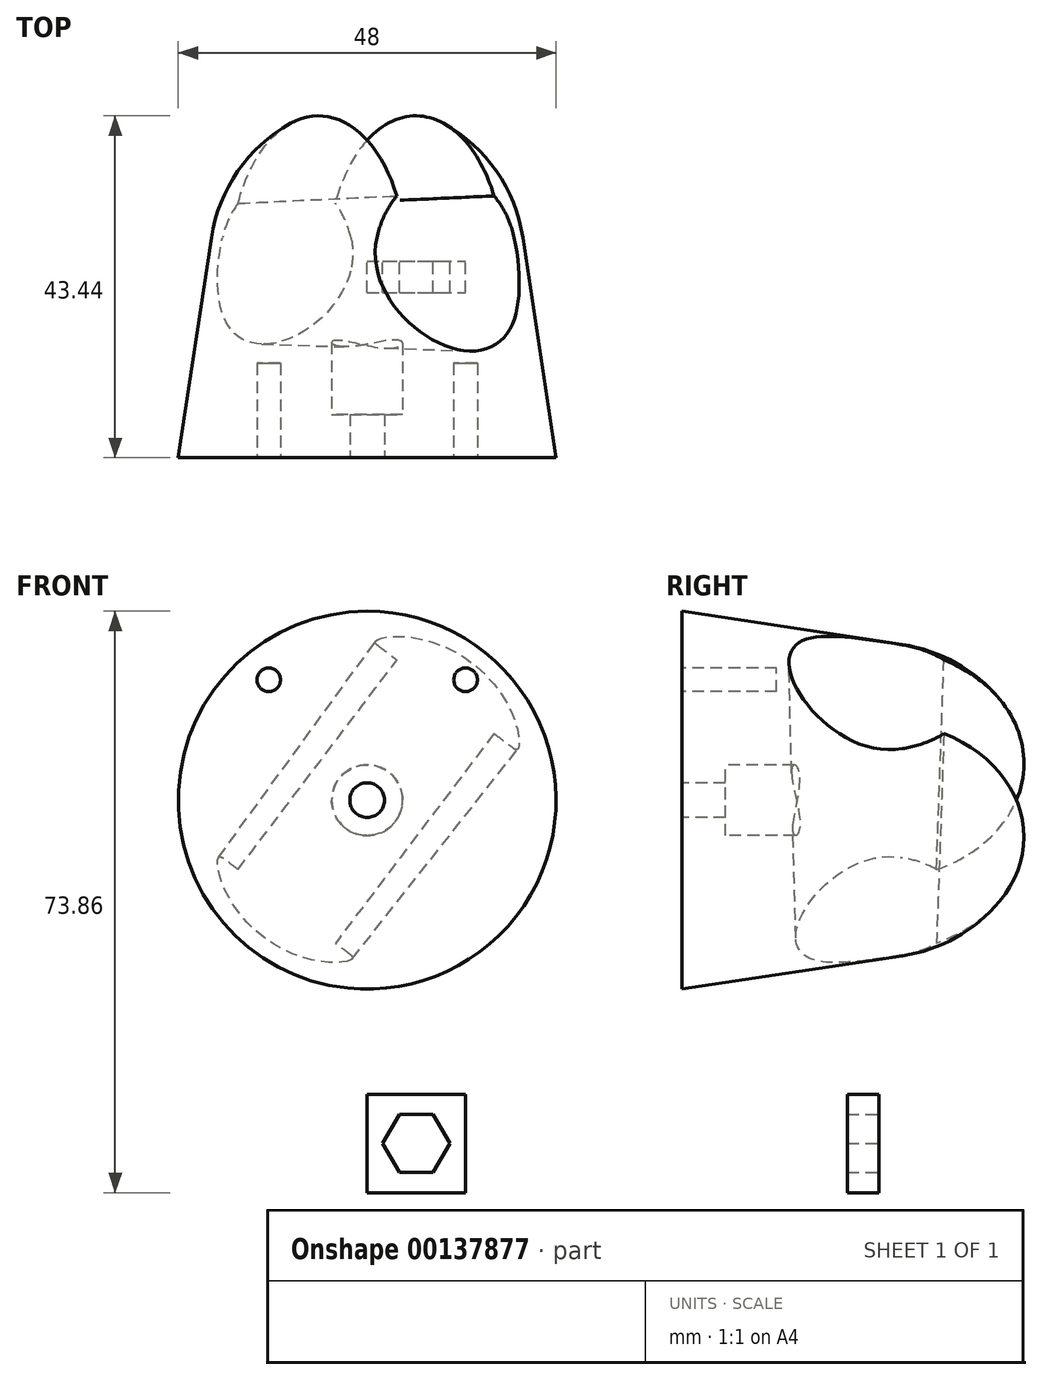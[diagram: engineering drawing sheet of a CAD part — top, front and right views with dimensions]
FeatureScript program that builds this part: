
annotation { "Feature Type Name" : "Feature", "Feature Type Description" : "" }
export const myFeature = defineFeature(function(context is Context, id is Id, definition is map)
    precondition{}
    {
        {
            var Q0;
            Q0=qCreatedBy(makeId("Front.planeOp"),FACE);
            var sketch = newSketch(context, id + "F0", { "sketchPlane" : qUnion([Q0])});
            skLineSegment(sketch, "E0", {"start": v(-15.1, -19.93) * mm, "end": v(15.1, 19.93) * mm});
            skLineSegment(sketch, "E1", {"start": v(15.1, 19.93) * mm, "end": v(5.93, 26.87) * mm});
            skLineSegment(sketch, "E2", {"start": v(5.93, 26.87) * mm, "end": v(-23.47, -13.59) * mm});
            skLineSegment(sketch, "E3", {"start": v(-23.47, -13.59) * mm, "end": v(-15.1, -19.93) * mm});
            skPoint(sketch, "E4", {"position": v(0, 0) * mm});
            skSolve(sketch);
        }
        {
            var Q0;
            Q0 = qSketchRegion(id + "F0", true);
            var Q1;
            Q1=sQuery(id+"F0.wireOp",EDGE,"E0");
            revolve(context, id + "F1", {"entities" : qUnion([Q0]), "axis" : qUnion([Q1]), "revolveType" : RevolveType.FULL});
        }
        {
            var Q0;
            Q0=qCreatedBy(makeId("Front.planeOp"),FACE);
            var sketch = newSketch(context, id + "F2", { "sketchPlane" : qUnion([Q0])});
            skLineSegment(sketch, "E5.0", {"start": v(24.26, 12.98) * mm, "end": v(5.93, 26.87) * mm, "construction": true});
            skLineSegment(sketch, "E6.0", {"start": v(-6.73, -26.27) * mm, "end": v(-23.47, -13.59) * mm, "construction": true});
            skLineSegment(sketch, "E7", {"start": v(15.1, 19.93) * mm, "end": v(-15.1, -19.93) * mm, "construction": true});
            skLineSegment(sketch, "E8", {"start": v(21.27, 15.25) * mm, "end": v(-8.92, -24.6) * mm});
            skLineSegment(sketch, "E9", {"start": v(-8.92, -24.6) * mm, "end": v(-21.27, -15.25) * mm});
            skLineSegment(sketch, "E10", {"start": v(-21.27, -15.25) * mm, "end": v(8.92, 24.6) * mm});
            skLineSegment(sketch, "E11", {"start": v(8.92, 24.6) * mm, "end": v(21.27, 15.25) * mm});
            skSolve(sketch);
        }
        {
            var Q0;
            Q0 = qSketchRegion(id + "F2", true);
            extrude(context, id + "F3", {"entities" : qUnion([Q0]), "operationType" : NewBodyOperationType.ADD, "oppositeDirection" : true, "depth" : 25 * mm});
        }
        {
            var Q0;
            Q0=qCreatedBy(makeId("Top.planeOp"),FACE);
            var sketch = newSketch(context, id + "F4", { "sketchPlane" : qUnion([Q0])});
            skLineSegment(sketch, "E12", {"start": v(0, -25) * mm, "end": v(24, -25) * mm});
            skLineSegment(sketch, "E13", {"start": v(24, -25) * mm, "end": v(19.78, 2.98) * mm});
            skArc(sketch, "E14", {"start": v(19.78, 2.98) * mm, "mid": v(13.04, 15.16) * mm, "end": v(0, 20) * mm});
            skLineSegment(sketch, "E15", {"start": v(0, 20) * mm, "end": v(0, -25) * mm});
            skSolve(sketch);
        }
        {
            var Q0;
            Q0 = qSketchRegion(id + "F4", true);
            var Q1;
            Q1=sQuery(id+"F4.wireOp",EDGE,"E15");
            revolve(context, id + "F5", {"entities" : qUnion([Q0]), "axis" : qUnion([Q1]), "revolveType" : RevolveType.FULL});
        }
        {
            var Q0;
            Q0=makeQuery(id+"F1.opRevolve","SWEPT_BODY",BODY,{"disambiguationData":[OSD([sQuery(id+"F0.wireOp",EDGE,"E0"),sQuery(id+"F0.wireOp",EDGE,"E1"),sQuery(id+"F0.wireOp",EDGE,"E2"),sQuery(id+"F0.wireOp",EDGE,"E3")])]});
            var Q1;
            Q1=makeQuery(id+"F5.opRevolve","SWEPT_BODY",BODY,{"disambiguationData":[OSD([sQuery(id+"F4.wireOp",EDGE,"E12"),sQuery(id+"F4.wireOp",EDGE,"E13"),sQuery(id+"F4.wireOp",EDGE,"E14"),sQuery(id+"F4.wireOp",EDGE,"E15")])]});
            booleanBodies(context, id + "F6", {"operationType" : BooleanOperationType.SUBTRACTION, "tools" : qUnion([Q0]), "targets" : qUnion([Q1])});
        }
        {
            var Q0;
            Q0=makeQuery(id+"F5.opRevolve","SWEPT_FACE",FACE,{"disambiguationData":[OSD([sQuery(id+"F4.wireOp",EDGE,"E12")])]});
            var sketch = newSketch(context, id + "F7", { "sketchPlane" : qUnion([Q0])});
            skCircle(sketch, "E16", {"center": v(0, 0) * mm, "radius": 2.2 * mm});
            skSolve(sketch);
        }
        {
            var Q0;
            Q0 = qSketchRegion(id + "F7", true);
            extrude(context, id + "F8", {"entities" : qUnion([Q0]), "operationType" : NewBodyOperationType.REMOVE, "oppositeDirection" : true, "depth" : 5.5 * mm});
        }
        {
            var Q0;
            Q0=makeQuery(id+"F8.boolean.opBoolean","COPY",FACE,{"derivedFrom":makeQuery(id+"F8.opExtrude","CAP_FACE",FACE,{"disambiguationData":[OSD([sQuery(id+"F7.wireOp",EDGE,"E16")])],"isStart":false})});
            var sketch = newSketch(context, id + "F9", { "sketchPlane" : qUnion([Q0])});
            skCircle(sketch, "E17", {"center": v(0, 0) * mm, "radius": 4.5 * mm});
            skSolve(sketch);
        }
        {
            var Q0;
            Q0 = qSketchRegion(id + "F9", true);
            extrude(context, id + "F10", {"entities" : qUnion([Q0]), "operationType" : NewBodyOperationType.REMOVE, "endBound" : BoundingType.THROUGH_ALL, "oppositeDirection" : true, "depth" : 25 * mm});
        }
        {
            var Q0;
            Q0=qCreatedBy(makeId("Front.planeOp"),FACE);
            var sketch = newSketch(context, id + "F11", { "sketchPlane" : qUnion([Q0])});
            skLineSegment(sketch, "E18.bottom", {"start": v(0, -49.86) * mm, "end": v(12.5, -49.86) * mm});
            skLineSegment(sketch, "E18.top", {"start": v(0, -37.36) * mm, "end": v(12.5, -37.36) * mm});
            skLineSegment(sketch, "E18.left", {"start": v(0, -49.86) * mm, "end": v(0, -37.36) * mm});
            skLineSegment(sketch, "E18.right", {"start": v(12.5, -49.86) * mm, "end": v(12.5, -37.36) * mm});
            skLineSegment(sketch, "E19", {"start": v(12.5, -43.6) * mm, "end": v(0, -43.6) * mm, "construction": true});
            skCircle(sketch, "E20.cCircle", {"center": v(6.25, -43.6) * mm, "radius": 3.7 * mm, "construction": true});
            skLineSegment(sketch, "E20.0", {"start": v(4.11, -39.9) * mm, "end": v(8.39, -39.9) * mm});
            skLineSegment(sketch, "E20.1", {"start": v(8.39, -39.9) * mm, "end": v(10.52, -43.6) * mm});
            skLineSegment(sketch, "E20.2", {"start": v(10.52, -43.6) * mm, "end": v(8.39, -47.3) * mm});
            skLineSegment(sketch, "E20.3", {"start": v(8.39, -47.3) * mm, "end": v(4.11, -47.3) * mm});
            skLineSegment(sketch, "E20.4", {"start": v(4.11, -47.3) * mm, "end": v(1.98, -43.6) * mm});
            skLineSegment(sketch, "E20.5", {"start": v(1.98, -43.6) * mm, "end": v(4.11, -39.9) * mm});
            skPoint(sketch, "E20.0.midPoint", {"position": v(6.25, -39.9) * mm});
            skSolve(sketch);
        }
        {
            var Q0;
            Q0 = qSketchRegion(id + "F11", true);
            extrude(context, id + "F12", {"entities" : qUnion([Q0]), "depth" : 4 * mm});
        }
        {
            var Q0;
            Q0=makeQuery(id+"F5.opRevolve","SWEPT_FACE",FACE,{"disambiguationData":[OSD([sQuery(id+"F4.wireOp",EDGE,"E12")])]});
            var sketch = newSketch(context, id + "F13", { "sketchPlane" : qUnion([Q0])});
            skCircle(sketch, "E21", {"center": v(0, 0) * mm, "radius": 22.5 * mm, "construction": true});
            skLineSegment(sketch, "E22", {"start": v(-9.75, 21.93) * mm, "end": v(-9.75, -21.93) * mm, "construction": true});
            skLineSegment(sketch, "E23.MirrorCS", {"start": v(9.75, 21.93) * mm, "end": v(9.75, -21.93) * mm, "construction": true});
            skCircle(sketch, "E24", {"center": v(-12.5, 15.3) * mm, "radius": 2.75 * mm, "construction": true});
            skCircle(sketch, "E25", {"center": v(-12.5, 15.3) * mm, "radius": 1.5 * mm});
            skCircle(sketch, "E26.MirrorC", {"center": v(12.5, 15.3) * mm, "radius": 1.5 * mm});
            skSolve(sketch);
        }
        {
            var Q0;
            Q0 = qSketchRegion(id + "F13", true);
            extrude(context, id + "F14", {"entities" : qUnion([Q0]), "operationType" : NewBodyOperationType.REMOVE, "oppositeDirection" : true, "depth" : 12 * mm});
        }
    });
